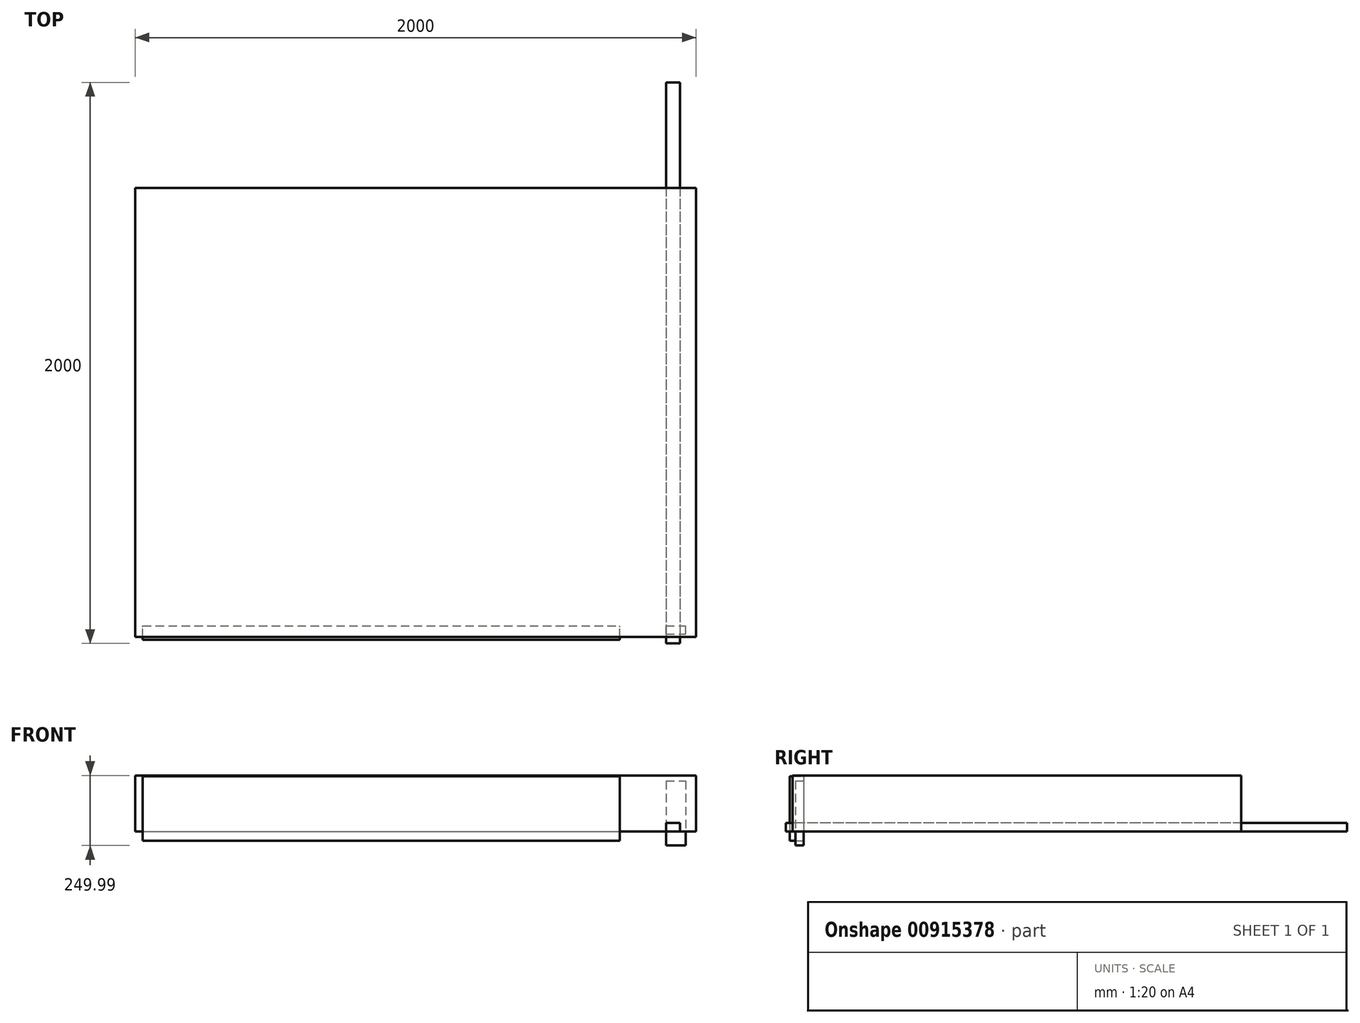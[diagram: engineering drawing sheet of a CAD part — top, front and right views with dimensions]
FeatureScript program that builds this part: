
annotation { "Feature Type Name" : "Feature", "Feature Type Description" : "" }
export const myFeature = defineFeature(function(context is Context, id is Id, definition is map)
    precondition{}
    {
        {
            var Q0;
            Q0=qCreatedBy(makeId("Front.planeOp"),FACE);
            var sketch = newSketch(context, id + "F0", { "sketchPlane" : qUnion([Q0])});
            skLineSegment(sketch, "E0.bottom", {"start": v(-1914.26, 196.7) * mm, "end": v(-214.26, 196.7) * mm});
            skLineSegment(sketch, "E0.top", {"start": v(-1914.26, -33.3) * mm, "end": v(-214.26, -33.3) * mm});
            skLineSegment(sketch, "E0.left", {"start": v(-1914.26, 196.7) * mm, "end": v(-1914.26, -33.3) * mm});
            skLineSegment(sketch, "E0.right", {"start": v(-214.26, 196.7) * mm, "end": v(-214.26, -33.3) * mm});
            skSolve(sketch);
        }
        {
            var Q0;
            Q0 = qSketchRegion(id + "F0", true);
            extrude(context, id + "F1", {"entities" : qUnion([Q0]), "depth" : 50 * mm, "offsetDistance" : 25 * mm});
        }
        {
            var Q0;
            Q0=qCreatedBy(makeId("Top.planeOp"),FACE);
            var sketch = newSketch(context, id + "F2", { "sketchPlane" : qUnion([Q0])});
            skLineSegment(sketch, "E1.bottom", {"start": v(-49.26, 1936.58) * mm, "end": v(0.74, 1936.58) * mm});
            skLineSegment(sketch, "E1.top", {"start": v(-49.26, -63.42) * mm, "end": v(0.74, -63.42) * mm});
            skLineSegment(sketch, "E1.left", {"start": v(-49.26, 1936.58) * mm, "end": v(-49.26, -63.42) * mm});
            skLineSegment(sketch, "E1.right", {"start": v(0.74, 1936.58) * mm, "end": v(0.74, -63.42) * mm});
            skSolve(sketch);
        }
        {
            var Q0;
            Q0 = qSketchRegion(id + "F2", true);
            extrude(context, id + "F3", {"entities" : qUnion([Q0]), "depth" : 30 * mm, "offsetDistance" : 25 * mm});
        }
        {
            var Q0;
            Q0=qCreatedBy(makeId("Front.planeOp"),FACE);
            var sketch = newSketch(context, id + "F4", { "sketchPlane" : qUnion([Q0])});
            skLineSegment(sketch, "E2.bottom", {"start": v(-49.26, 180.01) * mm, "end": v(20.74, 180.01) * mm});
            skLineSegment(sketch, "E2.top", {"start": v(-49.26, -49.99) * mm, "end": v(20.74, -49.99) * mm});
            skLineSegment(sketch, "E2.left", {"start": v(-49.26, 180.01) * mm, "end": v(-49.26, -49.99) * mm});
            skLineSegment(sketch, "E2.right", {"start": v(20.74, 180.01) * mm, "end": v(20.74, -49.99) * mm});
            skSolve(sketch);
        }
        {
            var Q0;
            Q0 = qSketchRegion(id + "F4", true);
            extrude(context, id + "F5", {"entities" : qUnion([Q0]), "depth" : 30 * mm, "offsetDistance" : 25 * mm});
        }
        {
            var Q0;
            Q0=qCreatedBy(makeId("Top.planeOp"),FACE);
            var sketch = newSketch(context, id + "F6", { "sketchPlane" : qUnion([Q0])});
            skLineSegment(sketch, "E3.bottom", {"start": v(-1941.66, 1559.63) * mm, "end": v(58.34, 1559.63) * mm});
            skLineSegment(sketch, "E3.top", {"start": v(-1941.66, -40.37) * mm, "end": v(58.34, -40.37) * mm});
            skLineSegment(sketch, "E3.left", {"start": v(-1941.66, 1559.63) * mm, "end": v(-1941.66, -40.37) * mm});
            skLineSegment(sketch, "E3.right", {"start": v(58.34, 1559.63) * mm, "end": v(58.34, -40.37) * mm});
            skSolve(sketch);
        }
        {
            var Q0;
            Q0 = qSketchRegion(id + "F6", true);
            extrude(context, id + "F7", {"entities" : qUnion([Q0]), "depth" : 200 * mm, "offsetDistance" : 25 * mm});
        }
    });
